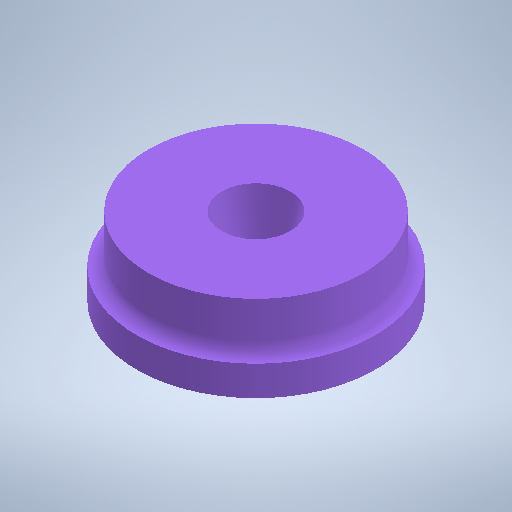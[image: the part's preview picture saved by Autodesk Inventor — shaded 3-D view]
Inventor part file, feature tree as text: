
AUTODESK INVENTOR PART (.ipt)
format: ipt  version: 2025 (Build 290162010, 162A)  size: 262,656 bytes
history: native  units: mm
features: revolve x2, sketch x2, plane x1
ambient origin geometry x8: Origin, YZ Plane, XZ Plane, XY Plane, X Axis, Y Axis, Z Axis, Center Point
bodies: Volumenkörper1 (feature_tree)
feature tree (5):
  revolve  "Umdrehung1"
  plane  "Arbeitsebene1"
  revolve  "Umdrehung2"
  sketch  "Skizze1"  dims[d0=5.0mm]
  sketch  "Skizze2"  dims[d2=40.0mm d3=36.0mm d4=90.0deg d5=0.0mm d6=1.5mm d7=2.094395mm d8=11.5mm d9=20.0mm d10=90.0deg d12=13.0mm]
